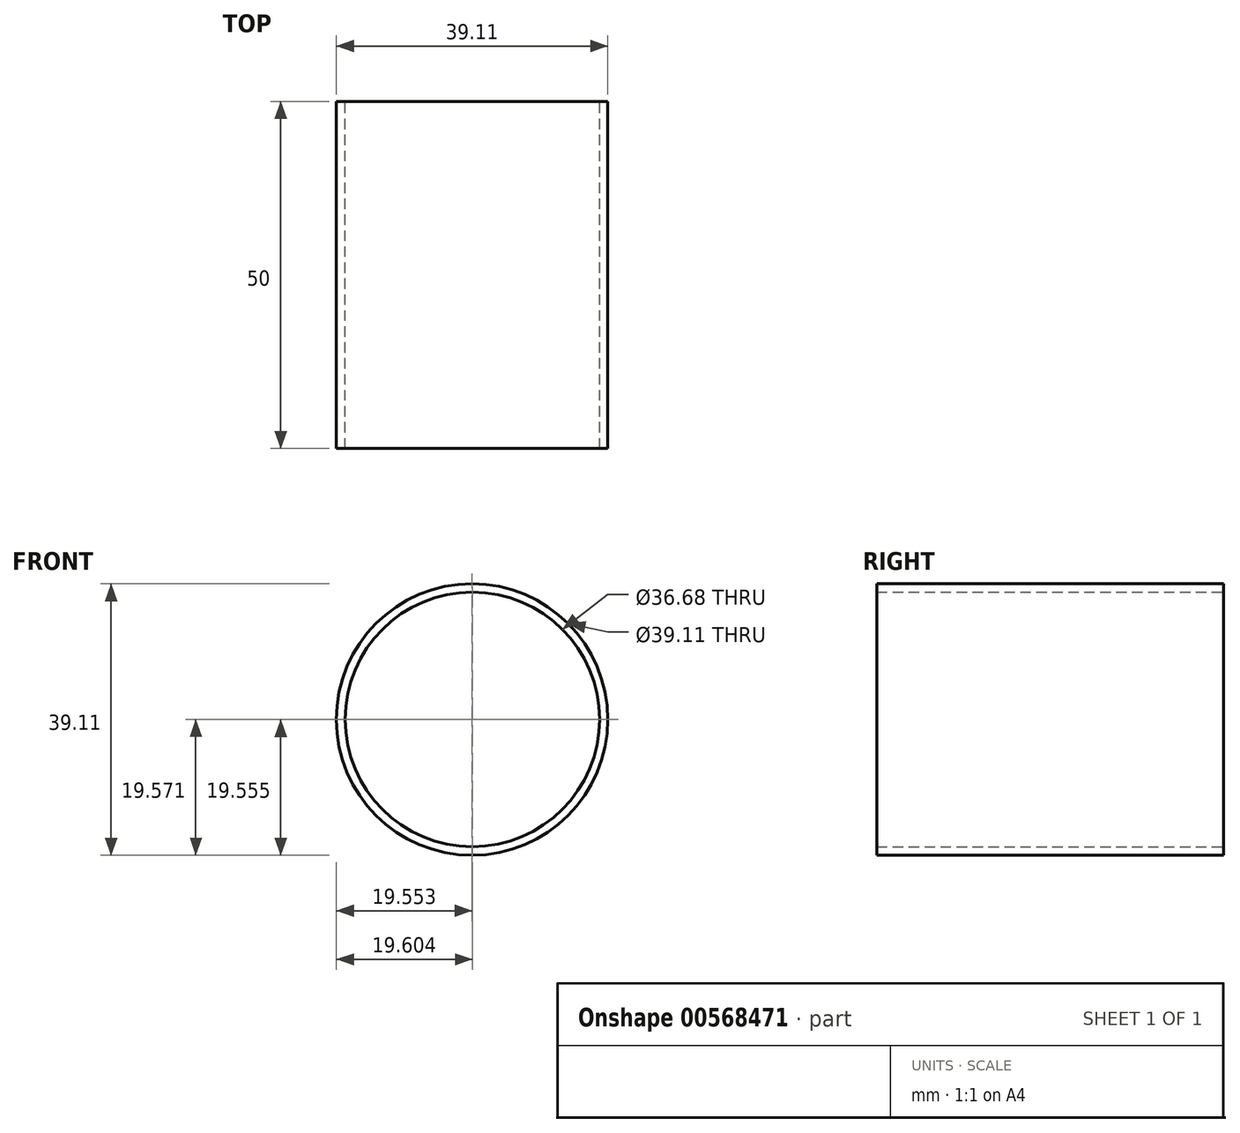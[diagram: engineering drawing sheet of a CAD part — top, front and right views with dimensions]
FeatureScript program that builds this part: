
annotation { "Feature Type Name" : "Feature", "Feature Type Description" : "" }
export const myFeature = defineFeature(function(context is Context, id is Id, definition is map)
    precondition{}
    {
        {
            var Q0;
            Q0=qCreatedBy(makeId("Front.planeOp"),FACE);
            var sketch = newSketch(context, id + "F0", { "sketchPlane" : qUnion([Q0])});
            skCircle(sketch, "E0", {"center": v(12.3, 38.34) * mm, "radius": 19.56 * mm});
            skSolve(sketch);
        }
        {
            var Q0;
            Q0=qCreatedBy(makeId("Front.planeOp"),FACE);
            var sketch = newSketch(context, id + "F1", { "sketchPlane" : qUnion([Q0])});
            skCircle(sketch, "E1", {"center": v(12.34, 38.36) * mm, "radius": 18.34 * mm});
            skSolve(sketch);
        }
        {
            var Q0;
            Q0=sQuery(id+"F1.wireOp",EDGE,"E1");
            extrude(context, id + "F2", {"bodyType" : ToolBodyType.SURFACE, "surfaceEntities" : qUnion([Q0]), "oppositeDirection" : true, "depth" : 50 * mm, "offsetDistance" : 25.4 * mm});
        }
        {
            var Q0;
            Q0=sQuery(id+"F0.wireOp",EDGE,"E0");
            extrude(context, id + "F3", {"bodyType" : ToolBodyType.SURFACE, "surfaceEntities" : qUnion([Q0]), "oppositeDirection" : true, "depth" : 50 * mm, "offsetDistance" : 25.4 * mm});
        }
    });
